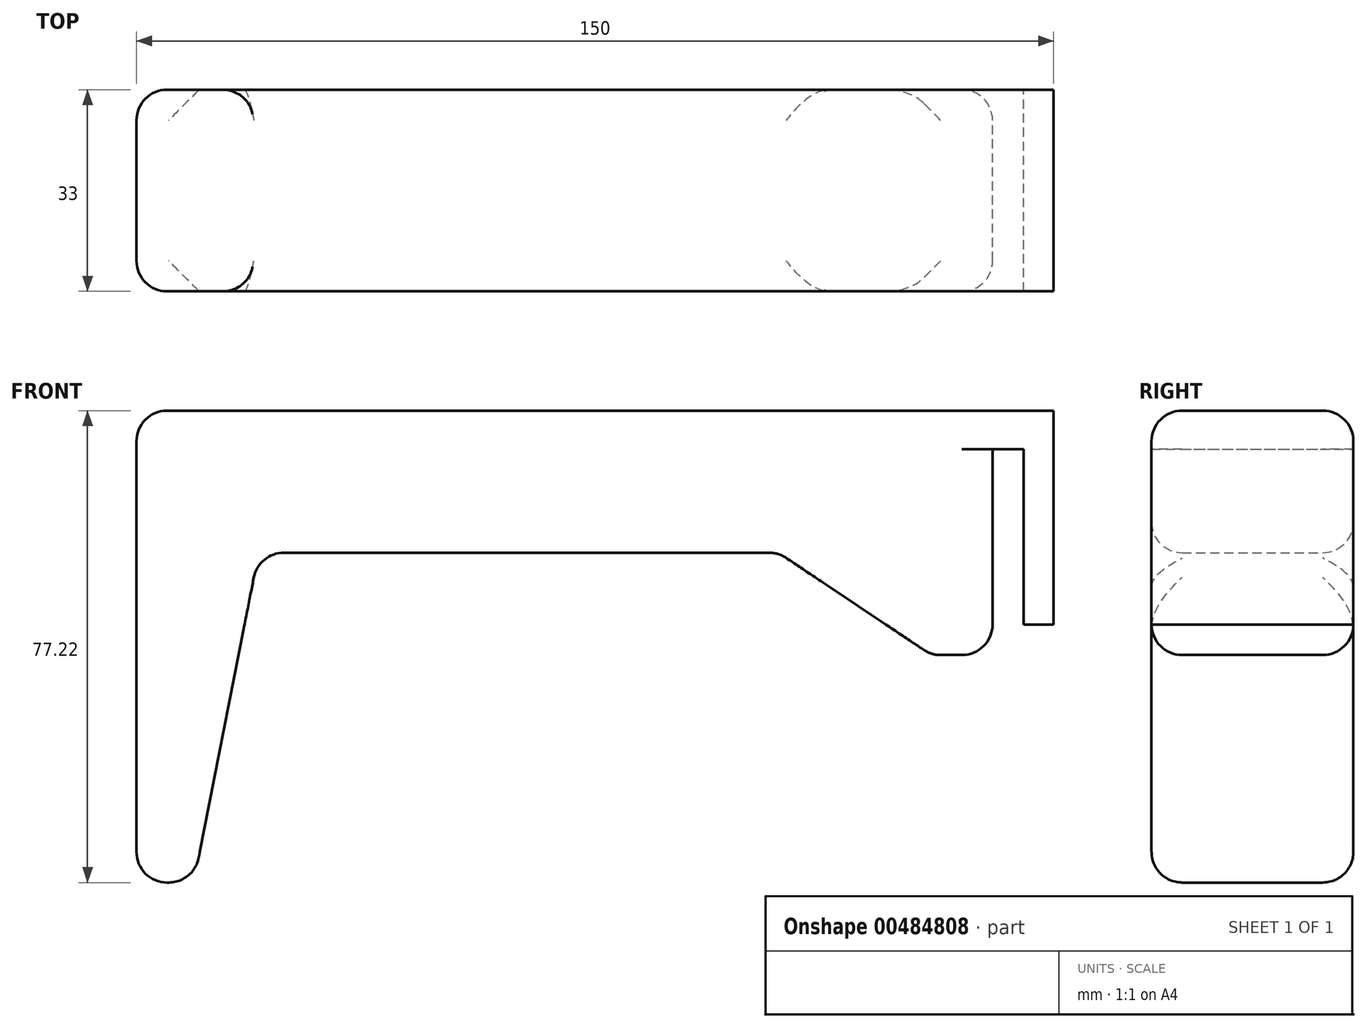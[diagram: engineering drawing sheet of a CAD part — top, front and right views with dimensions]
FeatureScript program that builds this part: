
annotation { "Feature Type Name" : "Feature", "Feature Type Description" : "" }
export const myFeature = defineFeature(function(context is Context, id is Id, definition is map)
    precondition{}
    {
        {
            var Q0;
            Q0=qCreatedBy(makeId("Front.planeOp"),FACE);
            var sketch = newSketch(context, id + "F0", { "sketchPlane" : qUnion([Q0])});
            skLineSegment(sketch, "E0", {"start": v(-95.64, 43.35) * mm, "end": v(-95.64, -33.87) * mm});
            skLineSegment(sketch, "E1", {"start": v(-95.64, -33.87) * mm, "end": v(-86.27, -33.87) * mm});
            skLineSegment(sketch, "E2", {"start": v(-86.27, -33.87) * mm, "end": v(-75.67, 20.1) * mm});
            skLineSegment(sketch, "E3", {"start": v(-75.67, 20.1) * mm, "end": v(9.33, 20.1) * mm});
            skLineSegment(sketch, "E4", {"start": v(9.33, 20.1) * mm, "end": v(34.36, 3.35) * mm});
            skLineSegment(sketch, "E5", {"start": v(34.36, 3.35) * mm, "end": v(44.36, 3.35) * mm});
            skLineSegment(sketch, "E6", {"start": v(44.36, 3.35) * mm, "end": v(44.36, 43.35) * mm});
            skLineSegment(sketch, "E7", {"start": v(44.36, 43.35) * mm, "end": v(-95.64, 43.35) * mm});
            skLineSegment(sketch, "E8", {"start": v(44.36, 43.35) * mm, "end": v(54.36, 43.35) * mm});
            skLineSegment(sketch, "E9", {"start": v(54.36, 43.35) * mm, "end": v(54.36, 8.35) * mm});
            skLineSegment(sketch, "E10", {"start": v(54.36, 8.35) * mm, "end": v(49.46, 8.35) * mm});
            skLineSegment(sketch, "E11", {"start": v(49.46, 8.35) * mm, "end": v(49.46, 37.02) * mm});
            skLineSegment(sketch, "E12", {"start": v(49.46, 37.02) * mm, "end": v(44.36, 37.02) * mm});
            skSolve(sketch);
        }
        {
            var Q0;
            Q0 = qSketchRegion(id + "F0", true);
            extrude(context, id + "F1", {"entities" : qUnion([Q0]), "depth" : 33 * mm});
        }
        {
            var Q0;
            Q0=makeQuery(id+"F1.opExtrude","SWEPT_FACE",FACE,{"disambiguationData":[OSD([sQuery(id+"F0.wireOp",EDGE,"E3")])]});
            var Q1;
            Q1=makeQuery(id+"F1.opExtrude","SWEPT_FACE",FACE,{"disambiguationData":[OSD([sQuery(id+"F0.wireOp",EDGE,"E1")])]});
            var Q2;
            Q2=makeQuery(id+"F1.opExtrude","SWEPT_FACE",FACE,{"disambiguationData":[OSD([sQuery(id+"F0.wireOp",EDGE,"E0")])]});
            var Q3;
            Q3=makeQuery(id+"F1.opExtrude","CAP_EDGE",EDGE,{"disambiguationData":[OSD([sQuery(id+"F0.wireOp",EDGE,"E7"),sQuery(id+"F0.wireOp",EDGE,"E8")])],"isStart":true});
            var Q4;
            Q4=makeQuery(id+"F1.opExtrude","CAP_EDGE",EDGE,{"disambiguationData":[OSD([sQuery(id+"F0.wireOp",EDGE,"E7"),sQuery(id+"F0.wireOp",EDGE,"E8")])],"isStart":false});
            var Q5;
            Q5=makeQuery(id+"F1.opExtrude","SWEPT_EDGE",EDGE,{"disambiguationData":[OSD([sQuery(id+"F0.wireOp",EDGE,"E4"),sQuery(id+"F0.wireOp",EDGE,"E5")])]});
            var Q6;
            Q6=makeQuery(id+"F1.opExtrude","CAP_EDGE",EDGE,{"disambiguationData":[OSD([sQuery(id+"F0.wireOp",EDGE,"E6")])],"isStart":false});
            var Q7;
            Q7=makeQuery(id+"F1.opExtrude","CAP_EDGE",EDGE,{"disambiguationData":[OSD([sQuery(id+"F0.wireOp",EDGE,"E6")])],"isStart":true});
            var Q8;
            Q8=makeQuery(id+"F1.opExtrude","SWEPT_FACE",FACE,{"disambiguationData":[OSD([sQuery(id+"F0.wireOp",EDGE,"E5")])]});
            fillet(context, id + "F2", {"entities" : qUnion([Q0, Q1, Q2, Q3, Q4, Q5, Q6, Q7, Q8]), "radius" : 5 * mm, "tangentPropagation" : true, "allowEdgeOverflow" : false});
        }
    });
